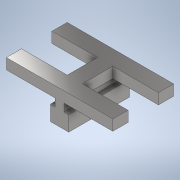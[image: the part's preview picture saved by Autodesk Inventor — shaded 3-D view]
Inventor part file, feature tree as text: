
AUTODESK INVENTOR PART (.ipt)
format: ipt  version: 2022 (Build 260153000, 153)  size: 161,280 bytes
history: native  units: in
note: dims shown in document units (in); Inventor stores cm internally (conversion verified against a paired STEP export)
features: extrude x2, sketch x2
ambient origin geometry x8: Origin, YZ Plane, XZ Plane, XY Plane, X Axis, Y Axis, Z Axis, Center Point
bodies: Solid1 (feature_tree)
feature tree (4):
  extrude  "Extrusion1"  Depth=3.937in
  extrude  "Extrusion2"  Depth=7.874in
  sketch  "Sketch1"  dims[d0=27.5591in d1=3.937in]
  sketch  "Sketch2"  dims[d2=11.811in d3=7.874in d4=3.937in d5=27.5591in d6=11.811in d7=2.7559in d8=0.0in d9=1.1811in d10=2.3622in d11=1.9685in d12=1.1811in d13=3.937in d14=4.7244in d15=1.1811in d16=15.748in d17=0.0in]
